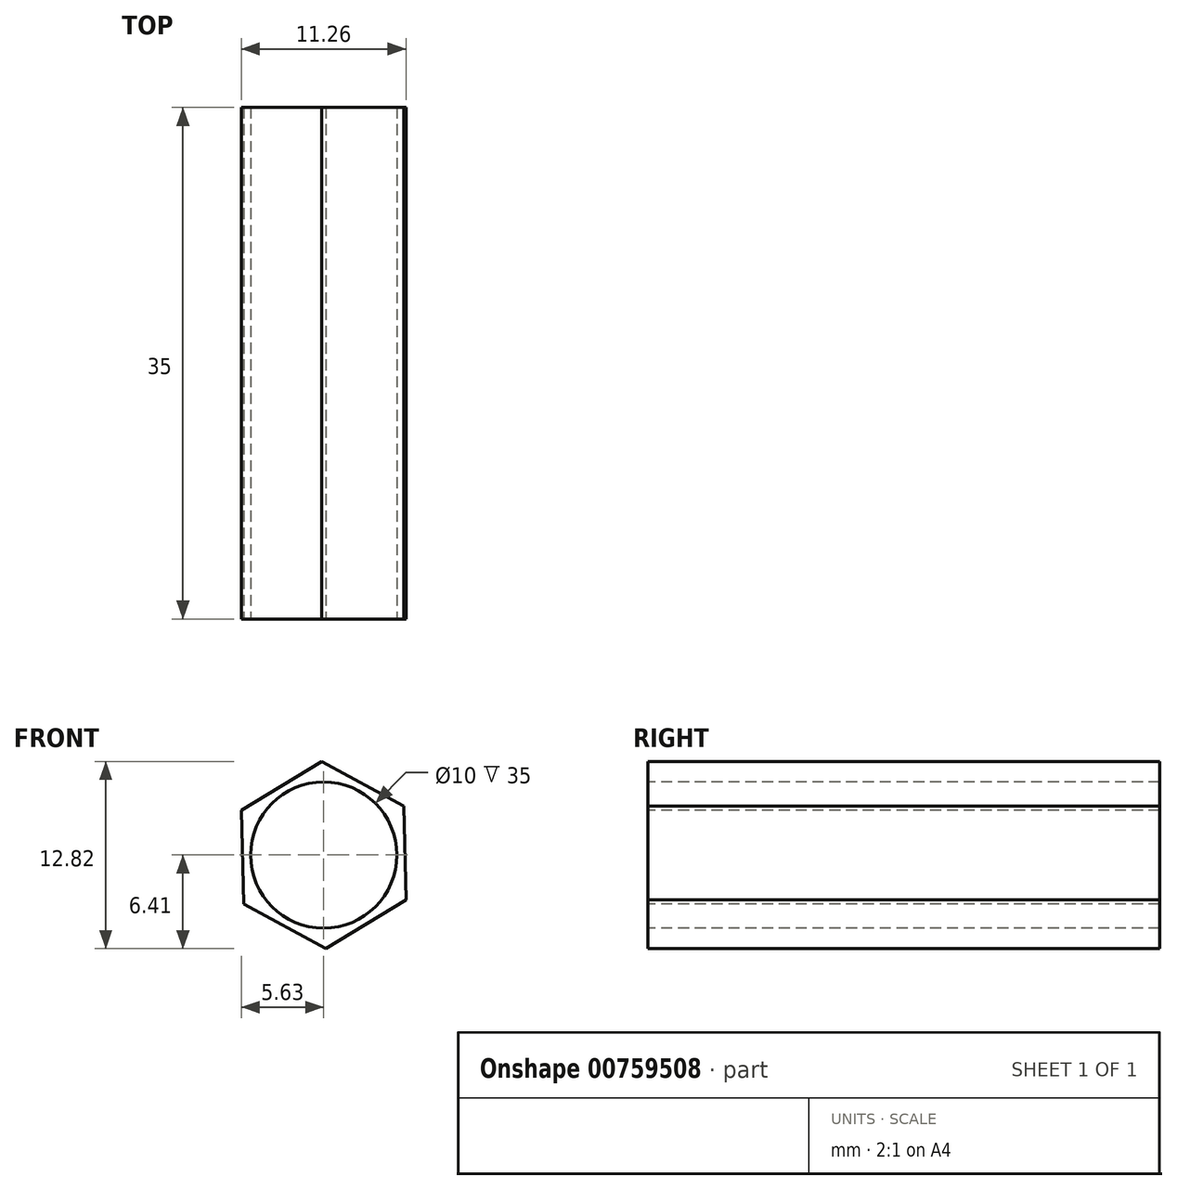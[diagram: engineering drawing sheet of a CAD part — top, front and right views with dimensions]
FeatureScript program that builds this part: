
annotation { "Feature Type Name" : "Feature", "Feature Type Description" : "" }
export const myFeature = defineFeature(function(context is Context, id is Id, definition is map)
    precondition{}
    {
        {
            var Q0;
            Q0=qCreatedBy(makeId("Front.planeOp"),FACE);
            var sketch = newSketch(context, id + "F0", { "sketchPlane" : qUnion([Q0])});
            skCircle(sketch, "E0.cCircle", {"center": v(0, 0) * mm, "radius": 5.56 * mm, "construction": true});
            skLineSegment(sketch, "E0.0", {"start": v(-5.63, 3.08) * mm, "end": v(-0.15, 6.41) * mm});
            skLineSegment(sketch, "E0.1", {"start": v(-0.15, 6.41) * mm, "end": v(5.48, 3.34) * mm});
            skLineSegment(sketch, "E0.2", {"start": v(5.48, 3.34) * mm, "end": v(5.63, -3.08) * mm});
            skLineSegment(sketch, "E0.3", {"start": v(5.63, -3.08) * mm, "end": v(0.15, -6.41) * mm});
            skLineSegment(sketch, "E0.4", {"start": v(0.15, -6.41) * mm, "end": v(-5.48, -3.34) * mm});
            skLineSegment(sketch, "E0.5", {"start": v(-5.48, -3.34) * mm, "end": v(-5.63, 3.08) * mm});
            skPoint(sketch, "E0.0.midPoint", {"position": v(-2.89, 4.74) * mm});
            skSolve(sketch);
        }
        {
            var Q0;
            Q0=makeQuery(id+"F0.imprint","IMPRINT",FACE,{"disambiguationData":[TD([[makeQuery(id+"F0.imprint","IMPRINT",EDGE,{"derivedFrom":sQuery(id+"F0.wireOp",EDGE,"E0.0")}),-1.0]])]});
            extrude(context, id + "F1", {"entities" : qUnion([Q0]), "oppositeDirection" : true, "depth" : 35 * mm, "offsetDistance" : 25 * mm});
        }
        {
            var Q0;
            Q0=qCreatedBy(makeId("Front.planeOp"),FACE);
            var sketch = newSketch(context, id + "F2", { "sketchPlane" : qUnion([Q0])});
            skCircle(sketch, "E1", {"center": v(0, 0) * mm, "radius": 5 * mm});
            skSolve(sketch);
        }
        {
            var Q0;
            Q0=makeQuery(id+"F2.imprint","IMPRINT",FACE,{"disambiguationData":[TD([[makeQuery(id+"F2.imprint","IMPRINT",EDGE,{"derivedFrom":sQuery(id+"F2.wireOp",EDGE,"E1")}),1.0]])]});
            extrude(context, id + "F3", {"entities" : qUnion([Q0]), "operationType" : NewBodyOperationType.REMOVE, "oppositeDirection" : true, "depth" : 35 * mm, "offsetDistance" : 25 * mm});
        }
    });
